FCSTD DOCUMENT  (FreeCAD 0.18R15684 (Git))
Label: polygon_with_hole
License: All rights reserved
LicenseURL: http://en.wikipedia.org/wiki/All_rights_reserved
objects: Sketcher::SketchObject×1, PartDesign::Body×1
note: 2 computed .brp shape members not serialized (recipe doc carries the construction recipe); baked Part::Feature solids carry a one-line shape summary decoded from their .brp

FEATURE [Sketcher::SketchObject] Sketch
  MapMode = 5
  Support = -> [XY_Plane]
  sketch-geometry (16):
    g0: LineSegment StartX=9.14 StartY=7.14 StartZ=0 EndX=-14.5656 EndY=5.26 EndZ=0
    g1: LineSegment StartX=-14.5656 StartY=5.26 StartZ=0 EndX=-19.7077 EndY=-6.42892 EndZ=0
    g2: LineSegment StartX=-19.7077 StartY=-6.42892 StartZ=0 EndX=-13.3275 EndY=-21.1345 EndZ=0
    g3: LineSegment StartX=-13.3275 StartY=-21.1345 StartZ=0 EndX=14.6376 EndY=-22.7203 EndZ=0
    g4: LineSegment StartX=14.6376 StartY=-22.7203 StartZ=0 EndX=30.8469 EndY=-10.0723 EndZ=0
    g5: LineSegment StartX=30.8469 StartY=-10.0723 StartZ=0 EndX=17.6614 EndY=2.26886 EndZ=0
    g6: LineSegment StartX=17.6614 StartY=2.26886 StartZ=0 EndX=18.1684 EndY=13.2472 EndZ=0
    g7: LineSegment StartX=18.1684 StartY=13.2472 StartZ=0 EndX=9.14 EndY=7.14 EndZ=0
    g8: LineSegment StartX=5.72103 StartY=16.9003 StartZ=0 EndX=29.0775 EndY=32.6994 EndZ=0
    g9: LineSegment StartX=29.0775 StartY=32.6994 StartZ=0 EndX=27.8636 EndY=6.41676 EndZ=0
    g10: LineSegment StartX=27.8636 StartY=6.41676 StartZ=0 EndX=46.2181 EndY=-10.7624 EndZ=0
    g11: LineSegment StartX=46.2181 StartY=-10.7624 StartZ=0 EndX=17.8251 EndY=-32.9171 EndZ=0
    g12: LineSegment StartX=17.8251 StartY=-32.9171 StartZ=0 EndX=-20.0478 EndY=-30.7695 EndZ=0
    g13: LineSegment StartX=-20.0478 StartY=-30.7695 StartZ=0 EndX=-30.6204 EndY=-6.4012 EndZ=0
    g14: LineSegment StartX=-30.6204 StartY=-6.4012 StartZ=0 EndX=-21.3128 EndY=14.7563 EndZ=0
    g15: LineSegment StartX=-21.3128 StartY=14.7563 StartZ=0 EndX=5.72103 EndY=16.9003 EndZ=0
  constraints (48):
    c: Coincident(g0,g1)
    c: Coincident(g1,g2)
    c: Coincident(g2,g3)
    c: Coincident(g3,g4)
    c: Coincident(g4,g5)
    c: Coincident(g5,g6)
    c: Coincident(g6,g7)
    c: Coincident(g7,g0)
    c: Coincident(g8,g9)
    c: Coincident(g9,g10)
    c: Coincident(g10,g11)
    c: Coincident(g11,g12)
    c: Coincident(g12,g13)
    c: Coincident(g13,g14)
    c: Coincident(g14,g15)
    c: Coincident(g15,g8)
    c: Parallel(g15,g0)
    c: Parallel(g7,g8)
    c: Parallel(g6,g9)
    c: Parallel(g5,g10)
    c: Parallel(g4,g11)
    c: Parallel(g3,g12)
    c: Parallel(g2,g13)
    c: Parallel(g14,g1)
    c: Distance(g0,g15) = 10
    c: Distance(g0) = 23.78
    c: Distance(g1) = 12.77
    c: Distance(g2) = 16.03
    c: Distance(g3) = 28.01
    c: Distance(g4) = 20.56
    c: Distance(g5) = 18.06
    c: Distance(g6) = 10.99
    c: Distance(g7) = 10.9
    c: DistanceY(g-1,g0) = 7.14
    c: DistanceX(g-1,g0) = 9.14
    c: DistanceY(g-1,g0) = 5.26
    c: Angle(g1,g0) = 2.06438
    c: Angle(g2,g1) = 2.3178
    c: Angle(g3,g2) = 2.0368
    c: Angle(g4,g3) = 2.42234
    c: Angle(g5,g4) = 1.41494
    c: Distance(g6,g9) = 10
    c: Distance(g4,g10) = 10
    c: Distance(g4,g11) = 10
    c: Distance(g11,g3) = 10
    c: Distance(g2,g13) = 10
    c: Distance(g1,g14) = 10
    c: Distance(g6,g8) = 10
FEATURE [PartDesign::Body] Body
  Group = -> [Sketch]
  Origin = -> Origin
